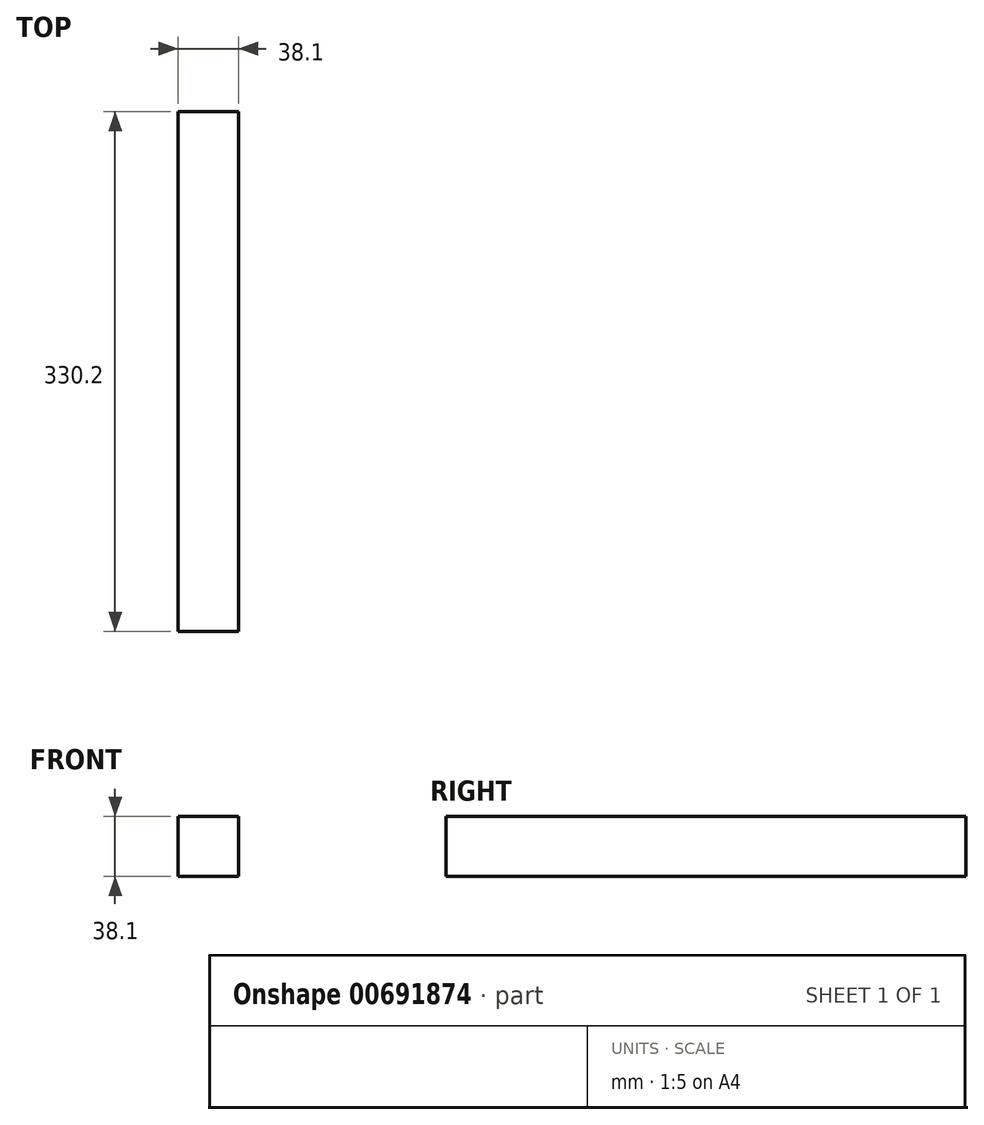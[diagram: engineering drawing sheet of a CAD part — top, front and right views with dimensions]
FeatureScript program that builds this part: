
annotation { "Feature Type Name" : "Feature", "Feature Type Description" : "" }
export const myFeature = defineFeature(function(context is Context, id is Id, definition is map)
    precondition{}
    {
        {
            var Q0;
            Q0=qCreatedBy(makeId("Front.planeOp"),FACE);
            var sketch = newSketch(context, id + "F0", { "sketchPlane" : qUnion([Q0])});
            skLineSegment(sketch, "E0.bottom", {"start": v(0, 0) * mm, "end": v(38.1, 0) * mm});
            skLineSegment(sketch, "E0.top", {"start": v(0, 38.1) * mm, "end": v(38.1, 38.1) * mm});
            skLineSegment(sketch, "E0.left", {"start": v(0, 0) * mm, "end": v(0, 38.1) * mm});
            skLineSegment(sketch, "E0.right", {"start": v(38.1, 0) * mm, "end": v(38.1, 38.1) * mm});
            skSolve(sketch);
        }
        {
            var Q0;
            Q0 = qSketchRegion(id + "F0", true);
            extrude(context, id + "F1", {"entities" : qUnion([Q0]), "depth" : 330.2 * mm, "offsetDistance" : 25.4 * mm});
        }
    });
